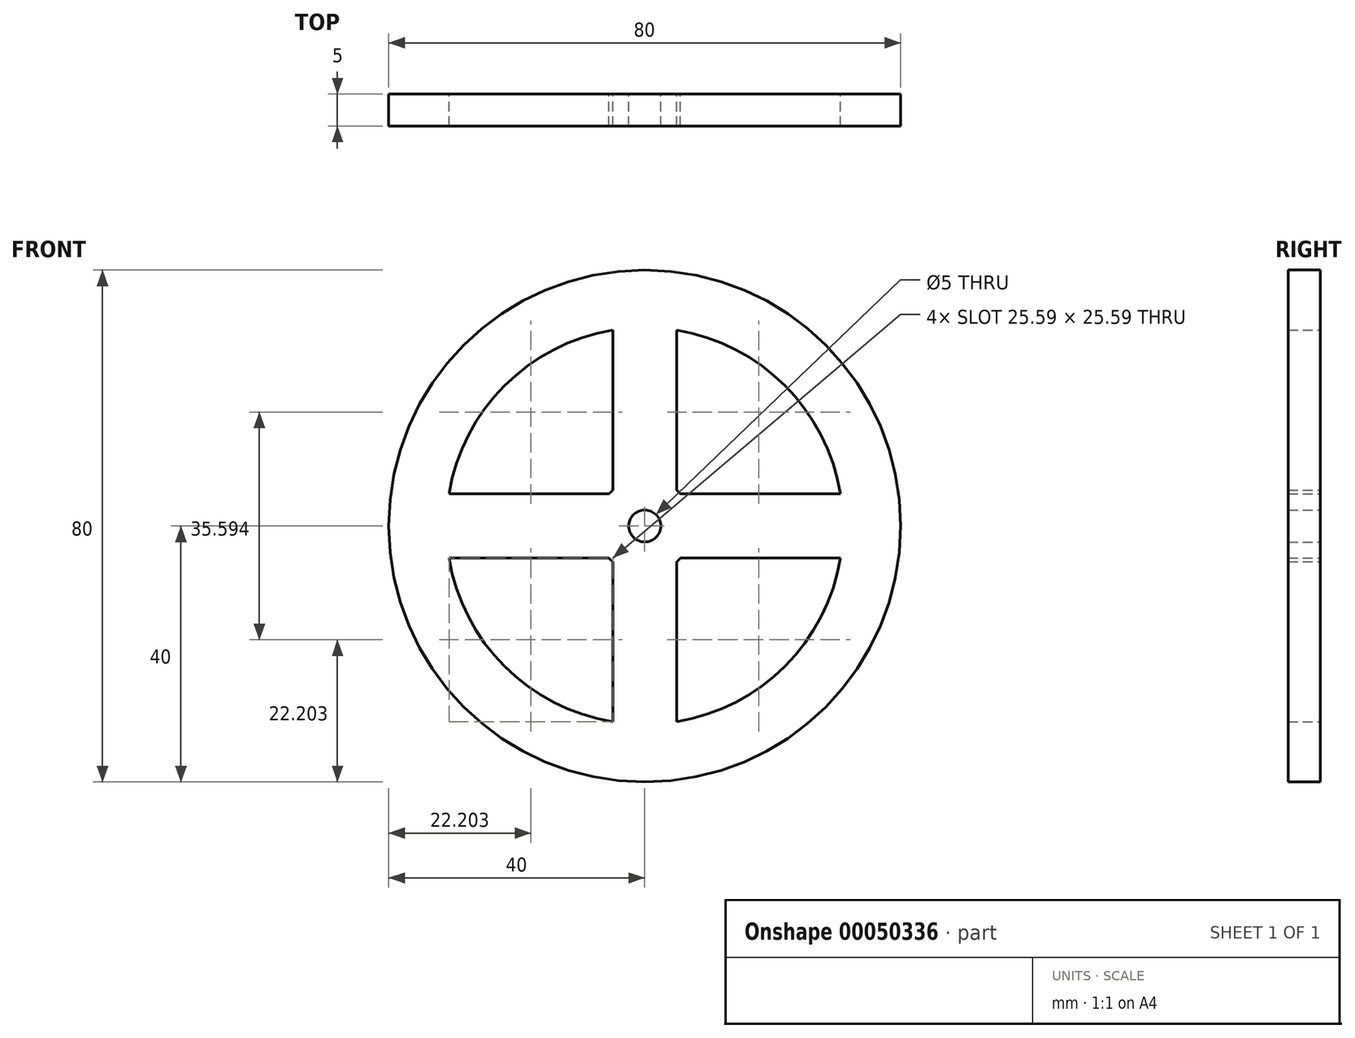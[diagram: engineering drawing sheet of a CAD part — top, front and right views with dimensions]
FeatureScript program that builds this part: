
annotation { "Feature Type Name" : "Feature", "Feature Type Description" : "" }
export const myFeature = defineFeature(function(context is Context, id is Id, definition is map)
    precondition{}
    {
        {
            var Q0;
            Q0=qCreatedBy(makeId("Front.planeOp"),FACE);
            var sketch = newSketch(context, id + "F0", { "sketchPlane" : qUnion([Q0])});
            skCircle(sketch, "E0", {"center": v(0, 0) * mm, "radius": 40 * mm});
            skArc(sketch, "E1", {"start": v(-30.6, -5) * mm, "mid": v(-21.92, -21.92) * mm, "end": v(-5, -30.6) * mm});
            skArc(sketch, "E2", {"start": v(5, -5.6) * mm, "mid": v(5.3, -5.3) * mm, "end": v(5.6, -5) * mm});
            skCircle(sketch, "E3", {"center": v(0, 0) * mm, "radius": 2.5 * mm});
            skLineSegment(sketch, "E4", {"start": v(0, 0) * mm, "end": v(0, 31) * mm, "construction": true});
            skLineSegment(sketch, "E5", {"start": v(0, 0) * mm, "end": v(31, 0) * mm, "construction": true});
            skLineSegment(sketch, "E6", {"start": v(0, 0) * mm, "end": v(0, -31) * mm, "construction": true});
            skLineSegment(sketch, "E7", {"start": v(0, 0) * mm, "end": v(-31, 0) * mm, "construction": true});
            skLineSegment(sketch, "E8.0", {"start": v(-5, 5.6) * mm, "end": v(-5, 30.6) * mm});
            skLineSegment(sketch, "E9.0", {"start": v(-5.6, 5) * mm, "end": v(-30.6, 5) * mm});
            skLineSegment(sketch, "E10.0", {"start": v(-5, -5.6) * mm, "end": v(-5, -30.6) * mm});
            skLineSegment(sketch, "E11.0", {"start": v(5, -5.6) * mm, "end": v(5, -30.6) * mm});
            skLineSegment(sketch, "E12.0", {"start": v(5.6, -5) * mm, "end": v(30.6, -5) * mm});
            skLineSegment(sketch, "E13.0", {"start": v(5.6, 5) * mm, "end": v(30.6, 5) * mm});
            skArc(sketch, "E14.trimOffspring", {"start": v(-5, 30.6) * mm, "mid": v(-21.92, 21.92) * mm, "end": v(-30.6, 5) * mm});
            skArc(sketch, "E15.trimOffspring", {"start": v(30.6, 5) * mm, "mid": v(21.92, 21.92) * mm, "end": v(5, 30.6) * mm});
            skArc(sketch, "E16.trimOffspring", {"start": v(5, -30.6) * mm, "mid": v(21.92, -21.92) * mm, "end": v(30.6, -5) * mm});
            skArc(sketch, "E17.trimOffspring", {"start": v(5.6, 5) * mm, "mid": v(5.3, 5.3) * mm, "end": v(5, 5.6) * mm});
            skArc(sketch, "E18.trimOffspring", {"start": v(-5.6, -5) * mm, "mid": v(-5.3, -5.3) * mm, "end": v(-5, -5.6) * mm});
            skArc(sketch, "E19.trimOffspring", {"start": v(-5, 5.6) * mm, "mid": v(-5.3, 5.3) * mm, "end": v(-5.6, 5) * mm});
            skLineSegment(sketch, "E20.trimOffspring", {"start": v(5, 5.6) * mm, "end": v(5, 30.6) * mm});
            skLineSegment(sketch, "E21.trimOffspring", {"start": v(-5.6, -5) * mm, "end": v(-30.6, -5) * mm});
            skSolve(sketch);
        }
        {
            var Q0;
            Q0=makeQuery(id+"F0.imprint","IMPRINT",FACE,{"disambiguationData":[TD([[makeQuery(id+"F0.imprint","IMPRINT",EDGE,{"derivedFrom":sQuery(id+"F0.wireOp",EDGE,"E0")}),1.0]])]});
            extrude(context, id + "F1", {"entities" : qUnion([Q0]), "endBound" : BoundingType.SYMMETRIC, "depth" : 5 * mm});
        }
    });
